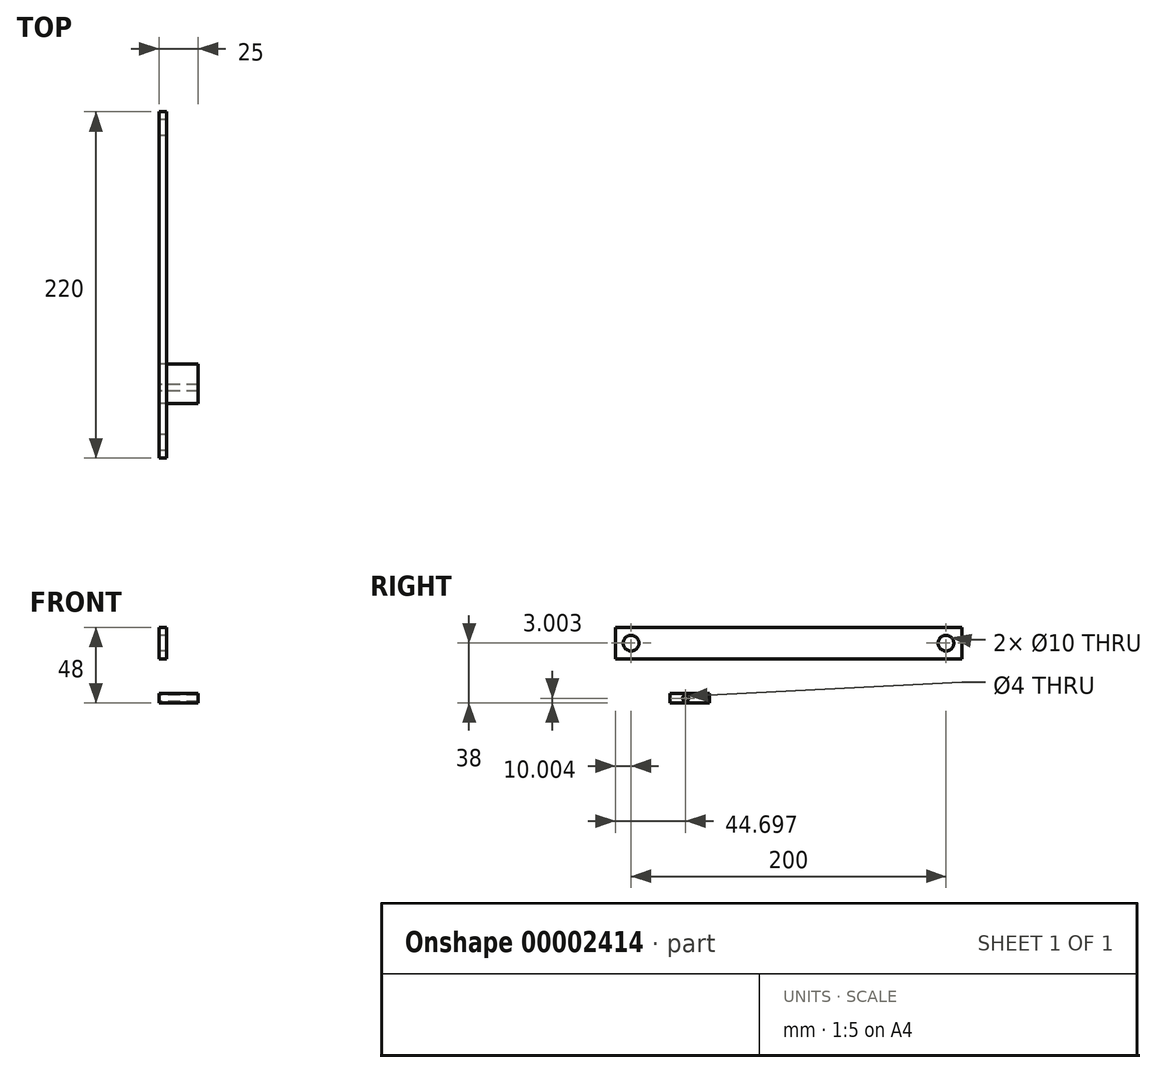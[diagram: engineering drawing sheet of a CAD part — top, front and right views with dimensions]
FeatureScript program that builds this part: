
annotation { "Feature Type Name" : "Feature", "Feature Type Description" : "" }
export const myFeature = defineFeature(function(context is Context, id is Id, definition is map)
    precondition{}
    {
        {
            var Q0;
            Q0=qCreatedBy(makeId("Right.planeOp"),FACE);
            var sketch = newSketch(context, id + "F0", { "sketchPlane" : qUnion([Q0])});
            skLineSegment(sketch, "E0.bottom", {"start": v(-80.89, 30.62) * mm, "end": v(139.11, 30.62) * mm});
            skLineSegment(sketch, "E0.top", {"start": v(-80.89, 10.62) * mm, "end": v(139.11, 10.62) * mm});
            skLineSegment(sketch, "E0.left", {"start": v(-80.89, 30.62) * mm, "end": v(-80.89, 10.62) * mm});
            skLineSegment(sketch, "E0.right", {"start": v(139.11, 30.62) * mm, "end": v(139.11, 10.62) * mm});
            skCircle(sketch, "E1", {"center": v(-70.89, 20.62) * mm, "radius": 5 * mm});
            skCircle(sketch, "E2", {"center": v(129.11, 20.62) * mm, "radius": 5 * mm});
            skSolve(sketch);
        }
        {
            var Q0;
            Q0=makeQuery(id+"F0.imprint","IMPRINT",FACE,{"disambiguationData":[TD([[makeQuery(id+"F0.imprint","IMPRINT",EDGE,{"derivedFrom":sQuery(id+"F0.wireOp",EDGE,"E0.bottom")}),-1.0]])]});
            extrude(context, id + "F1", {"entities" : qUnion([Q0]), "depth" : 5 * mm});
        }
        {
            var Q0;
            Q0=qCreatedBy(makeId("Right.planeOp"),FACE);
            var sketch = newSketch(context, id + "F2", { "sketchPlane" : qUnion([Q0])});
            skLineSegment(sketch, "E3.bottom", {"start": v(-46.2, -11.38) * mm, "end": v(-21.2, -11.38) * mm});
            skLineSegment(sketch, "E3.top", {"start": v(-46.2, -17.38) * mm, "end": v(-21.2, -17.38) * mm});
            skLineSegment(sketch, "E3.left", {"start": v(-46.2, -11.38) * mm, "end": v(-46.2, -17.38) * mm});
            skLineSegment(sketch, "E3.right", {"start": v(-21.2, -11.38) * mm, "end": v(-21.2, -17.38) * mm});
            skCircle(sketch, "E4", {"center": v(-36.2, -14.38) * mm, "radius": 2 * mm});
            skSolve(sketch);
        }
        {
            var Q0;
            Q0=makeQuery(id+"F2.imprint","IMPRINT",FACE,{"disambiguationData":[TD([[makeQuery(id+"F2.imprint","IMPRINT",EDGE,{"derivedFrom":sQuery(id+"F2.wireOp",EDGE,"E3.top")}),1.0]])]});
            extrude(context, id + "F3", {"entities" : qUnion([Q0]), "depth" : 25 * mm});
        }
    });
